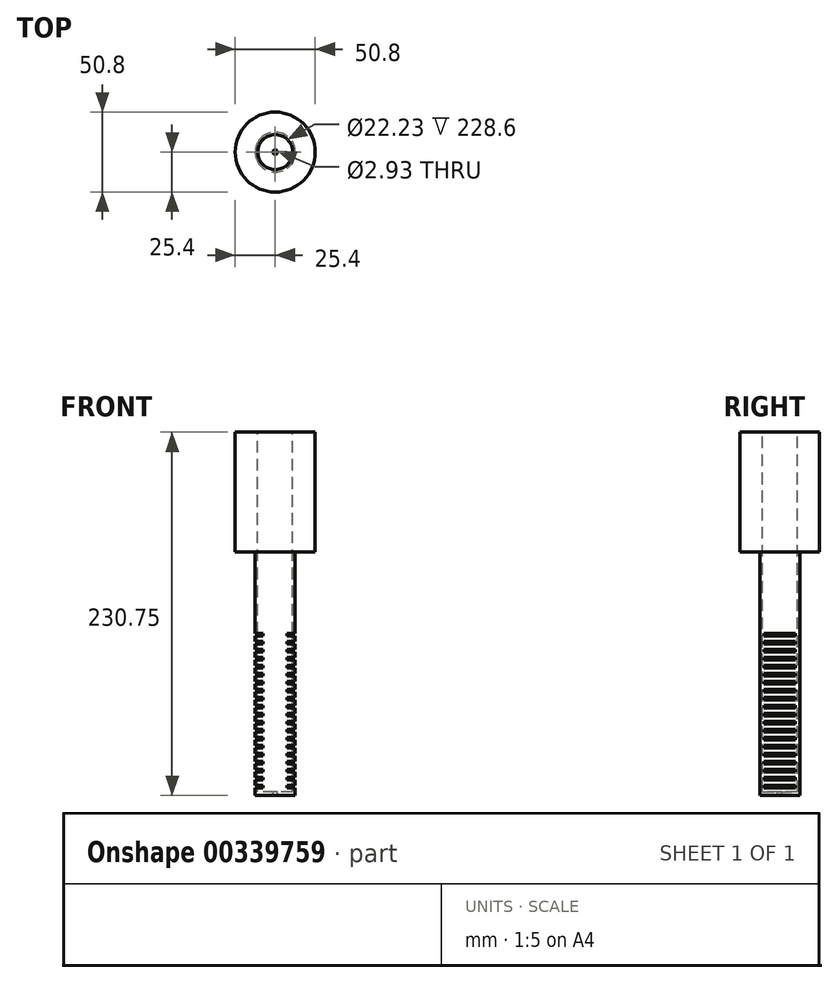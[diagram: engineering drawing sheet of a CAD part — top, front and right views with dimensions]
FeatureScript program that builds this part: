
annotation { "Feature Type Name" : "Feature", "Feature Type Description" : "" }
export const myFeature = defineFeature(function(context is Context, id is Id, definition is map)
    precondition{}
    {
        {
            var Q0;
            Q0=qCreatedBy(makeId("Front.planeOp"),FACE);
            var sketch = newSketch(context, id + "F0", { "sketchPlane" : qUnion([Q0])});
            skLineSegment(sketch, "E0", {"start": v(0, 228.6) * mm, "end": v(25.4, 228.6) * mm});
            skLineSegment(sketch, "E1", {"start": v(25.4, 228.6) * mm, "end": v(25.4, 152.4) * mm});
            skLineSegment(sketch, "E2", {"start": v(25.4, 152.4) * mm, "end": v(0, 152.4) * mm});
            skLineSegment(sketch, "E3", {"start": v(12.7, 0) * mm, "end": v(12.7, 152.4) * mm});
            skLineSegment(sketch, "E4", {"start": v(0, 152.4) * mm, "end": v(0, 228.6) * mm, "construction": true});
            skLineSegment(sketch, "E5", {"start": v(12.7, 0) * mm, "end": v(11.11, 0) * mm});
            skLineSegment(sketch, "E6", {"start": v(11.11, 0) * mm, "end": v(11.11, 152.4) * mm});
            skLineSegment(sketch, "E7", {"start": v(0, 152.4) * mm, "end": v(0, 0) * mm, "construction": true});
            skLineSegment(sketch, "E8", {"start": v(0, 0) * mm, "end": v(11.11, 0) * mm, "construction": true});
            skLineSegment(sketch, "E9", {"start": v(11.11, 0) * mm, "end": v(1.46, 0) * mm});
            skLineSegment(sketch, "E10", {"start": v(1.46, -2.15) * mm, "end": v(12.7, -2.15) * mm});
            skLineSegment(sketch, "E11", {"start": v(12.7, -2.15) * mm, "end": v(12.7, 0) * mm});
            skLineSegment(sketch, "E12", {"start": v(1.46, -2.15) * mm, "end": v(1.46, 0) * mm});
            skLineSegment(sketch, "E13", {"start": v(11.11, 152.4) * mm, "end": v(11.11, 228.6) * mm});
            skPoint(sketch, "E13.endSnap0", {"position": v(12.7, 228.6) * mm});
            skSolve(sketch);
        }
        {
            var Q0;
            Q0=makeQuery(id+"F0.imprint","IMPRINT",FACE,{"disambiguationData":[TD([[makeQuery(id+"F0.imprint","IMPRINT",EDGE,{"derivedFrom":sQuery(id+"F0.wireOp",EDGE,"E0")}),-1.0]])]});
            var Q1;
            Q1=makeQuery(id+"F0.imprint","IMPRINT",FACE,{"disambiguationData":[TD([[makeQuery(id+"F0.imprint","IMPRINT",EDGE,{"derivedFrom":sQuery(id+"F0.wireOp",EDGE,"E5")}),1.0]])]});
            var Q2;
            {var subQ0=sQuery(id+"F0.wireOp",EDGE,"E3");Q2=makeQuery(id+"F0.imprint","IMPRINT",FACE,{"disambiguationData":[TD([[makeQuery(id+"F0.imprint","IMPRINT",EDGE,{"derivedFrom":subQ0}),1.0]])]});}
            var Q3;
            Q3 = qConstructionFilter(qBodyType(qCreatedBy(id + "F0" ,EDGE), BodyType.WIRE), ConstructionObject.NO);
            var Q4;
            Q4=sQuery(id+"F0.wireOp",EDGE,"E7");
            revolve(context, id + "F1", {"entities" : qUnion([Q0, Q1, Q2]), "surfaceEntities" : qUnion([Q3]), "axis" : qUnion([Q4]), "revolveType" : RevolveType.FULL});
        }
        {
            var Q0;
            Q0=qCreatedBy(makeId("Front.planeOp"),FACE);
            var sketch = newSketch(context, id + "F2", { "sketchPlane" : qUnion([Q0])});
            skLineSegment(sketch, "E14.bottom", {"start": v(19.92, 2.54) * mm, "end": v(7.62, 2.54) * mm});
            skLineSegment(sketch, "E14.top", {"start": v(19.92, 4.13) * mm, "end": v(7.62, 4.13) * mm});
            skLineSegment(sketch, "E14.left", {"start": v(19.92, 2.54) * mm, "end": v(19.92, 4.13) * mm});
            skLineSegment(sketch, "E14.right", {"start": v(7.62, 2.54) * mm, "end": v(7.62, 4.13) * mm});
            skLineSegment(sketch, "E15.0.1.0", {"start": v(19.92, 9.2) * mm, "end": v(7.62, 9.2) * mm});
            skLineSegment(sketch, "E15.0.1.1", {"start": v(19.92, 7.62) * mm, "end": v(7.62, 7.62) * mm});
            skLineSegment(sketch, "E15.0.1.2", {"start": v(7.62, 7.62) * mm, "end": v(7.62, 9.2) * mm});
            skLineSegment(sketch, "E15.0.1.3", {"start": v(19.92, 7.62) * mm, "end": v(19.92, 9.2) * mm});
            skLineSegment(sketch, "E15.0.2.0", {"start": v(19.92, 14.29) * mm, "end": v(7.62, 14.29) * mm});
            skLineSegment(sketch, "E15.0.2.1", {"start": v(19.92, 12.7) * mm, "end": v(7.62, 12.7) * mm});
            skLineSegment(sketch, "E15.0.2.2", {"start": v(7.62, 12.7) * mm, "end": v(7.62, 14.29) * mm});
            skLineSegment(sketch, "E15.0.2.3", {"start": v(19.92, 12.7) * mm, "end": v(19.92, 14.29) * mm});
            skLineSegment(sketch, "E15.0.3.0", {"start": v(19.92, 19.37) * mm, "end": v(7.62, 19.37) * mm});
            skLineSegment(sketch, "E15.0.3.1", {"start": v(19.92, 17.78) * mm, "end": v(7.62, 17.78) * mm});
            skLineSegment(sketch, "E15.0.3.2", {"start": v(7.62, 17.78) * mm, "end": v(7.62, 19.37) * mm});
            skLineSegment(sketch, "E15.0.3.3", {"start": v(19.92, 17.78) * mm, "end": v(19.92, 19.37) * mm});
            skLineSegment(sketch, "E15.0.4.0", {"start": v(19.92, 24.45) * mm, "end": v(7.62, 24.45) * mm});
            skLineSegment(sketch, "E15.0.4.1", {"start": v(19.92, 22.86) * mm, "end": v(7.62, 22.86) * mm});
            skLineSegment(sketch, "E15.0.4.2", {"start": v(7.62, 22.86) * mm, "end": v(7.62, 24.45) * mm});
            skLineSegment(sketch, "E15.0.4.3", {"start": v(19.92, 22.86) * mm, "end": v(19.92, 24.45) * mm});
            skLineSegment(sketch, "E15.0.5.0", {"start": v(19.92, 29.53) * mm, "end": v(7.62, 29.53) * mm});
            skLineSegment(sketch, "E15.0.5.1", {"start": v(19.92, 27.94) * mm, "end": v(7.62, 27.94) * mm});
            skLineSegment(sketch, "E15.0.5.2", {"start": v(7.62, 27.94) * mm, "end": v(7.62, 29.53) * mm});
            skLineSegment(sketch, "E15.0.5.3", {"start": v(19.92, 27.94) * mm, "end": v(19.92, 29.53) * mm});
            skLineSegment(sketch, "E15.0.6.0", {"start": v(19.92, 34.6) * mm, "end": v(7.62, 34.6) * mm});
            skLineSegment(sketch, "E15.0.6.1", {"start": v(19.92, 33.02) * mm, "end": v(7.62, 33.02) * mm});
            skLineSegment(sketch, "E15.0.6.2", {"start": v(7.62, 33.02) * mm, "end": v(7.62, 34.6) * mm});
            skLineSegment(sketch, "E15.0.6.3", {"start": v(19.92, 33.02) * mm, "end": v(19.92, 34.6) * mm});
            skLineSegment(sketch, "E15.0.7.0", {"start": v(19.92, 39.69) * mm, "end": v(7.62, 39.69) * mm});
            skLineSegment(sketch, "E15.0.7.1", {"start": v(19.92, 38.1) * mm, "end": v(7.62, 38.1) * mm});
            skLineSegment(sketch, "E15.0.7.2", {"start": v(7.62, 38.1) * mm, "end": v(7.62, 39.69) * mm});
            skLineSegment(sketch, "E15.0.7.3", {"start": v(19.92, 38.1) * mm, "end": v(19.92, 39.69) * mm});
            skLineSegment(sketch, "E15.0.8.0", {"start": v(19.92, 44.77) * mm, "end": v(7.62, 44.77) * mm});
            skLineSegment(sketch, "E15.0.8.1", {"start": v(19.92, 43.18) * mm, "end": v(7.62, 43.18) * mm});
            skLineSegment(sketch, "E15.0.8.2", {"start": v(7.62, 43.18) * mm, "end": v(7.62, 44.77) * mm});
            skLineSegment(sketch, "E15.0.8.3", {"start": v(19.92, 43.18) * mm, "end": v(19.92, 44.77) * mm});
            skLineSegment(sketch, "E15.0.9.0", {"start": v(19.92, 49.85) * mm, "end": v(7.62, 49.85) * mm});
            skLineSegment(sketch, "E15.0.9.1", {"start": v(19.92, 48.26) * mm, "end": v(7.62, 48.26) * mm});
            skLineSegment(sketch, "E15.0.9.2", {"start": v(7.62, 48.26) * mm, "end": v(7.62, 49.85) * mm});
            skLineSegment(sketch, "E15.0.9.3", {"start": v(19.92, 48.26) * mm, "end": v(19.92, 49.85) * mm});
            skLineSegment(sketch, "E15.0.10.0", {"start": v(19.92, 54.93) * mm, "end": v(7.62, 54.93) * mm});
            skLineSegment(sketch, "E15.0.10.1", {"start": v(19.92, 53.34) * mm, "end": v(7.62, 53.34) * mm});
            skLineSegment(sketch, "E15.0.10.2", {"start": v(7.62, 53.34) * mm, "end": v(7.62, 54.93) * mm});
            skLineSegment(sketch, "E15.0.10.3", {"start": v(19.92, 53.34) * mm, "end": v(19.92, 54.93) * mm});
            skLineSegment(sketch, "E15.0.11.0", {"start": v(19.92, 60) * mm, "end": v(7.62, 60) * mm});
            skLineSegment(sketch, "E15.0.11.1", {"start": v(19.92, 58.42) * mm, "end": v(7.62, 58.42) * mm});
            skLineSegment(sketch, "E15.0.11.2", {"start": v(7.62, 58.42) * mm, "end": v(7.62, 60) * mm});
            skLineSegment(sketch, "E15.0.11.3", {"start": v(19.92, 58.42) * mm, "end": v(19.92, 60) * mm});
            skLineSegment(sketch, "E15.0.12.0", {"start": v(19.92, 65.09) * mm, "end": v(7.62, 65.09) * mm});
            skLineSegment(sketch, "E15.0.12.1", {"start": v(19.92, 63.5) * mm, "end": v(7.62, 63.5) * mm});
            skLineSegment(sketch, "E15.0.12.2", {"start": v(7.62, 63.5) * mm, "end": v(7.62, 65.09) * mm});
            skLineSegment(sketch, "E15.0.12.3", {"start": v(19.92, 63.5) * mm, "end": v(19.92, 65.09) * mm});
            skLineSegment(sketch, "E15.0.13.0", {"start": v(19.92, 70.17) * mm, "end": v(7.62, 70.17) * mm});
            skLineSegment(sketch, "E15.0.13.1", {"start": v(19.92, 68.58) * mm, "end": v(7.62, 68.58) * mm});
            skLineSegment(sketch, "E15.0.13.2", {"start": v(7.62, 68.58) * mm, "end": v(7.62, 70.17) * mm});
            skLineSegment(sketch, "E15.0.13.3", {"start": v(19.92, 68.58) * mm, "end": v(19.92, 70.17) * mm});
            skLineSegment(sketch, "E15.0.14.0", {"start": v(19.92, 75.25) * mm, "end": v(7.62, 75.25) * mm});
            skLineSegment(sketch, "E15.0.14.1", {"start": v(19.92, 73.66) * mm, "end": v(7.62, 73.66) * mm});
            skLineSegment(sketch, "E15.0.14.2", {"start": v(7.62, 73.66) * mm, "end": v(7.62, 75.25) * mm});
            skLineSegment(sketch, "E15.0.14.3", {"start": v(19.92, 73.66) * mm, "end": v(19.92, 75.25) * mm});
            skLineSegment(sketch, "E15.0.15.0", {"start": v(19.92, 80.33) * mm, "end": v(7.62, 80.33) * mm});
            skLineSegment(sketch, "E15.0.15.1", {"start": v(19.92, 78.74) * mm, "end": v(7.62, 78.74) * mm});
            skLineSegment(sketch, "E15.0.15.2", {"start": v(7.62, 78.74) * mm, "end": v(7.62, 80.33) * mm});
            skLineSegment(sketch, "E15.0.15.3", {"start": v(19.92, 78.74) * mm, "end": v(19.92, 80.33) * mm});
            skLineSegment(sketch, "E15.0.16.0", {"start": v(19.92, 85.4) * mm, "end": v(7.62, 85.4) * mm});
            skLineSegment(sketch, "E15.0.16.1", {"start": v(19.92, 83.82) * mm, "end": v(7.62, 83.82) * mm});
            skLineSegment(sketch, "E15.0.16.2", {"start": v(7.62, 83.82) * mm, "end": v(7.62, 85.4) * mm});
            skLineSegment(sketch, "E15.0.16.3", {"start": v(19.92, 83.82) * mm, "end": v(19.92, 85.4) * mm});
            skLineSegment(sketch, "E15.0.17.0", {"start": v(19.92, 90.49) * mm, "end": v(7.62, 90.49) * mm});
            skLineSegment(sketch, "E15.0.17.1", {"start": v(19.92, 88.9) * mm, "end": v(7.62, 88.9) * mm});
            skLineSegment(sketch, "E15.0.17.2", {"start": v(7.62, 88.9) * mm, "end": v(7.62, 90.49) * mm});
            skLineSegment(sketch, "E15.0.17.3", {"start": v(19.92, 88.9) * mm, "end": v(19.92, 90.49) * mm});
            skLineSegment(sketch, "E15.0.18.0", {"start": v(19.92, 95.57) * mm, "end": v(7.62, 95.57) * mm});
            skLineSegment(sketch, "E15.0.18.1", {"start": v(19.92, 93.98) * mm, "end": v(7.62, 93.98) * mm});
            skLineSegment(sketch, "E15.0.18.2", {"start": v(7.62, 93.98) * mm, "end": v(7.62, 95.57) * mm});
            skLineSegment(sketch, "E15.0.18.3", {"start": v(19.92, 93.98) * mm, "end": v(19.92, 95.57) * mm});
            skLineSegment(sketch, "E15.0.19.0", {"start": v(19.92, 100.65) * mm, "end": v(7.62, 100.65) * mm});
            skLineSegment(sketch, "E15.0.19.1", {"start": v(19.92, 99.06) * mm, "end": v(7.62, 99.06) * mm});
            skLineSegment(sketch, "E15.0.19.2", {"start": v(7.62, 99.06) * mm, "end": v(7.62, 100.65) * mm});
            skLineSegment(sketch, "E15.0.19.3", {"start": v(19.92, 99.06) * mm, "end": v(19.92, 100.65) * mm});
            skLineSegment(sketch, "E15.direction1", {"start": v(7.62, 2.54) * mm, "end": v(33.02, 2.54) * mm, "construction": true});
            skLineSegment(sketch, "E15.direction2", {"start": v(7.62, 2.54) * mm, "end": v(7.62, 7.62) * mm, "construction": true});
            skLineSegment(sketch, "E16.MirrorCS", {"start": v(-7.62, 38.1) * mm, "end": v(-7.62, 39.69) * mm});
            skLineSegment(sketch, "E17.MirrorCS", {"start": v(-7.62, 48.26) * mm, "end": v(-7.62, 49.85) * mm});
            skLineSegment(sketch, "E18.MirrorCS", {"start": v(-19.92, 78.74) * mm, "end": v(-19.92, 80.33) * mm});
            skLineSegment(sketch, "E19.MirrorCS", {"start": v(-19.92, 27.94) * mm, "end": v(-19.92, 29.53) * mm});
            skLineSegment(sketch, "E20.MirrorCS", {"start": v(-19.92, 17.78) * mm, "end": v(-19.92, 19.37) * mm});
            skLineSegment(sketch, "E21.MirrorCS", {"start": v(-7.62, 2.54) * mm, "end": v(-7.62, 4.13) * mm});
            skLineSegment(sketch, "E22.MirrorCS", {"start": v(-19.92, 12.7) * mm, "end": v(-19.92, 14.29) * mm});
            skLineSegment(sketch, "E23.MirrorCS", {"start": v(-19.92, 93.98) * mm, "end": v(-19.92, 95.57) * mm});
            skLineSegment(sketch, "E24.MirrorCS", {"start": v(-19.92, 73.66) * mm, "end": v(-19.92, 75.25) * mm});
            skLineSegment(sketch, "E25.MirrorCS", {"start": v(-19.92, 53.34) * mm, "end": v(-19.92, 54.93) * mm});
            skLineSegment(sketch, "E26.MirrorCS", {"start": v(-19.92, 33.02) * mm, "end": v(-19.92, 34.6) * mm});
            skLineSegment(sketch, "E27.MirrorCS", {"start": v(-7.62, 99.06) * mm, "end": v(-7.62, 100.65) * mm});
            skLineSegment(sketch, "E28.MirrorCS", {"start": v(-7.62, 78.74) * mm, "end": v(-7.62, 80.33) * mm});
            skLineSegment(sketch, "E29.MirrorCS", {"start": v(-7.62, 58.42) * mm, "end": v(-7.62, 60) * mm});
            skLineSegment(sketch, "E30.MirrorCS", {"start": v(-19.92, 38.1) * mm, "end": v(-19.92, 39.69) * mm});
            skLineSegment(sketch, "E31.MirrorCS", {"start": v(-7.62, 27.94) * mm, "end": v(-7.62, 29.53) * mm});
            skLineSegment(sketch, "E32.MirrorCS", {"start": v(-7.62, 88.9) * mm, "end": v(-7.62, 90.49) * mm});
            skLineSegment(sketch, "E33.MirrorCS", {"start": v(-7.62, 68.58) * mm, "end": v(-7.62, 70.17) * mm});
            skLineSegment(sketch, "E34.MirrorCS", {"start": v(-19.92, 58.42) * mm, "end": v(-19.92, 60) * mm});
            skLineSegment(sketch, "E35.MirrorCS", {"start": v(-19.92, 88.9) * mm, "end": v(-19.92, 90.49) * mm});
            skLineSegment(sketch, "E36.MirrorCS", {"start": v(-19.92, 68.58) * mm, "end": v(-19.92, 70.17) * mm});
            skLineSegment(sketch, "E37.MirrorCS", {"start": v(-19.92, 48.26) * mm, "end": v(-19.92, 49.85) * mm});
            skLineSegment(sketch, "E38.MirrorCS", {"start": v(-7.62, 2.54) * mm, "end": v(-33.02, 2.54) * mm, "construction": true});
            skLineSegment(sketch, "E39.MirrorCS", {"start": v(-7.62, 2.54) * mm, "end": v(-7.62, 7.62) * mm, "construction": true});
            skLineSegment(sketch, "E40.MirrorCS", {"start": v(-7.62, 17.78) * mm, "end": v(-7.62, 19.37) * mm});
            skLineSegment(sketch, "E41.MirrorCS", {"start": v(-7.62, 7.62) * mm, "end": v(-7.62, 9.2) * mm});
            skLineSegment(sketch, "E42.MirrorCS", {"start": v(-19.92, 7.62) * mm, "end": v(-19.92, 9.2) * mm});
            skLineSegment(sketch, "E43.MirrorCS", {"start": v(-7.62, 12.7) * mm, "end": v(-7.62, 14.29) * mm});
            skLineSegment(sketch, "E44.MirrorCS", {"start": v(-7.62, 43.18) * mm, "end": v(-7.62, 44.77) * mm});
            skLineSegment(sketch, "E45.MirrorCS", {"start": v(-7.62, 22.86) * mm, "end": v(-7.62, 24.45) * mm});
            skLineSegment(sketch, "E46.MirrorCS", {"start": v(-7.62, 83.82) * mm, "end": v(-7.62, 85.4) * mm});
            skLineSegment(sketch, "E47.MirrorCS", {"start": v(-7.62, 63.5) * mm, "end": v(-7.62, 65.09) * mm});
            skLineSegment(sketch, "E48.MirrorCS", {"start": v(-7.62, 93.98) * mm, "end": v(-7.62, 95.57) * mm});
            skLineSegment(sketch, "E49.MirrorCS", {"start": v(-7.62, 73.66) * mm, "end": v(-7.62, 75.25) * mm});
            skLineSegment(sketch, "E50.MirrorCS", {"start": v(-7.62, 53.34) * mm, "end": v(-7.62, 54.93) * mm});
            skLineSegment(sketch, "E51.MirrorCS", {"start": v(-7.62, 33.02) * mm, "end": v(-7.62, 34.6) * mm});
            skLineSegment(sketch, "E52.MirrorCS", {"start": v(-19.92, 43.18) * mm, "end": v(-19.92, 44.77) * mm});
            skLineSegment(sketch, "E53.MirrorCS", {"start": v(-19.92, 22.86) * mm, "end": v(-19.92, 24.45) * mm});
            skLineSegment(sketch, "E54.MirrorCS", {"start": v(-19.92, 83.82) * mm, "end": v(-19.92, 85.4) * mm});
            skLineSegment(sketch, "E55.MirrorCS", {"start": v(-19.92, 63.5) * mm, "end": v(-19.92, 65.09) * mm});
            skLineSegment(sketch, "E56.MirrorCS", {"start": v(-19.92, 99.06) * mm, "end": v(-19.92, 100.65) * mm});
            skLineSegment(sketch, "E57.MirrorCS", {"start": v(-19.92, 2.54) * mm, "end": v(-19.92, 4.13) * mm});
            skLineSegment(sketch, "E58.MirrorCS", {"start": v(-19.92, 2.54) * mm, "end": v(-7.62, 2.54) * mm});
            skLineSegment(sketch, "E59.MirrorCS", {"start": v(-19.92, 4.13) * mm, "end": v(-7.62, 4.13) * mm});
            skLineSegment(sketch, "E60.MirrorCS", {"start": v(-19.92, 38.1) * mm, "end": v(-7.62, 38.1) * mm});
            skLineSegment(sketch, "E61.MirrorCS", {"start": v(-19.92, 49.85) * mm, "end": v(-7.62, 49.85) * mm});
            skLineSegment(sketch, "E62.MirrorCS", {"start": v(-19.92, 29.53) * mm, "end": v(-7.62, 29.53) * mm});
            skLineSegment(sketch, "E63.MirrorCS", {"start": v(-19.92, 99.06) * mm, "end": v(-7.62, 99.06) * mm});
            skLineSegment(sketch, "E64.MirrorCS", {"start": v(-19.92, 90.49) * mm, "end": v(-7.62, 90.49) * mm});
            skLineSegment(sketch, "E65.MirrorCS", {"start": v(-19.92, 78.74) * mm, "end": v(-7.62, 78.74) * mm});
            skLineSegment(sketch, "E66.MirrorCS", {"start": v(-19.92, 58.42) * mm, "end": v(-7.62, 58.42) * mm});
            skLineSegment(sketch, "E67.MirrorCS", {"start": v(-19.92, 70.17) * mm, "end": v(-7.62, 70.17) * mm});
            skLineSegment(sketch, "E68.MirrorCS", {"start": v(-19.92, 100.65) * mm, "end": v(-7.62, 100.65) * mm});
            skLineSegment(sketch, "E69.MirrorCS", {"start": v(-19.92, 80.33) * mm, "end": v(-7.62, 80.33) * mm});
            skLineSegment(sketch, "E70.MirrorCS", {"start": v(-19.92, 60) * mm, "end": v(-7.62, 60) * mm});
            skLineSegment(sketch, "E71.MirrorCS", {"start": v(-19.92, 39.69) * mm, "end": v(-7.62, 39.69) * mm});
            skLineSegment(sketch, "E72.MirrorCS", {"start": v(-19.92, 48.26) * mm, "end": v(-7.62, 48.26) * mm});
            skLineSegment(sketch, "E73.MirrorCS", {"start": v(-19.92, 27.94) * mm, "end": v(-7.62, 27.94) * mm});
            skLineSegment(sketch, "E74.MirrorCS", {"start": v(-19.92, 88.9) * mm, "end": v(-7.62, 88.9) * mm});
            skLineSegment(sketch, "E75.MirrorCS", {"start": v(-19.92, 68.58) * mm, "end": v(-7.62, 68.58) * mm});
            skLineSegment(sketch, "E76.MirrorCS", {"start": v(-19.92, 85.4) * mm, "end": v(-7.62, 85.4) * mm});
            skLineSegment(sketch, "E77.MirrorCS", {"start": v(-19.92, 65.09) * mm, "end": v(-7.62, 65.09) * mm});
            skLineSegment(sketch, "E78.MirrorCS", {"start": v(-19.92, 44.77) * mm, "end": v(-7.62, 44.77) * mm});
            skLineSegment(sketch, "E79.MirrorCS", {"start": v(-19.92, 24.45) * mm, "end": v(-7.62, 24.45) * mm});
            skLineSegment(sketch, "E80.MirrorCS", {"start": v(-19.92, 95.57) * mm, "end": v(-7.62, 95.57) * mm});
            skLineSegment(sketch, "E81.MirrorCS", {"start": v(-19.92, 54.93) * mm, "end": v(-7.62, 54.93) * mm});
            skLineSegment(sketch, "E82.MirrorCS", {"start": v(-19.92, 75.25) * mm, "end": v(-7.62, 75.25) * mm});
            skLineSegment(sketch, "E83.MirrorCS", {"start": v(-19.92, 34.6) * mm, "end": v(-7.62, 34.6) * mm});
            skLineSegment(sketch, "E84.MirrorCS", {"start": v(-19.92, 43.18) * mm, "end": v(-7.62, 43.18) * mm});
            skLineSegment(sketch, "E85.MirrorCS", {"start": v(-19.92, 22.86) * mm, "end": v(-7.62, 22.86) * mm});
            skLineSegment(sketch, "E86.MirrorCS", {"start": v(-19.92, 83.82) * mm, "end": v(-7.62, 83.82) * mm});
            skLineSegment(sketch, "E87.MirrorCS", {"start": v(-19.92, 63.5) * mm, "end": v(-7.62, 63.5) * mm});
            skLineSegment(sketch, "E88.MirrorCS", {"start": v(-19.92, 17.78) * mm, "end": v(-7.62, 17.78) * mm});
            skLineSegment(sketch, "E89.MirrorCS", {"start": v(-19.92, 9.2) * mm, "end": v(-7.62, 9.2) * mm});
            skLineSegment(sketch, "E90.MirrorCS", {"start": v(-19.92, 7.62) * mm, "end": v(-7.62, 7.62) * mm});
            skLineSegment(sketch, "E91.MirrorCS", {"start": v(-19.92, 14.29) * mm, "end": v(-7.62, 14.29) * mm});
            skLineSegment(sketch, "E92.MirrorCS", {"start": v(-19.92, 12.7) * mm, "end": v(-7.62, 12.7) * mm});
            skLineSegment(sketch, "E93.MirrorCS", {"start": v(-19.92, 93.98) * mm, "end": v(-7.62, 93.98) * mm});
            skLineSegment(sketch, "E94.MirrorCS", {"start": v(-19.92, 73.66) * mm, "end": v(-7.62, 73.66) * mm});
            skLineSegment(sketch, "E95.MirrorCS", {"start": v(-19.92, 53.34) * mm, "end": v(-7.62, 53.34) * mm});
            skLineSegment(sketch, "E96.MirrorCS", {"start": v(-19.92, 33.02) * mm, "end": v(-7.62, 33.02) * mm});
            skLineSegment(sketch, "E97.MirrorCS", {"start": v(-19.92, 19.37) * mm, "end": v(-7.62, 19.37) * mm});
            skSolve(sketch);
        }
        {
            var Q0;
            Q0 = qSketchRegion(id + "F2", true);
            extrude(context, id + "F3", {"entities" : qUnion([Q0]), "operationType" : NewBodyOperationType.REMOVE, "endBound" : BoundingType.THROUGH_ALL, "depth" : 25.4 * mm, "hasSecondDirection" : true, "secondDirectionBound" : SecondDirectionBoundingType.THROUGH_ALL, "secondDirectionOppositeDirection" : true, "secondDirectionDepth" : 25.4 * mm});
        }
    });
